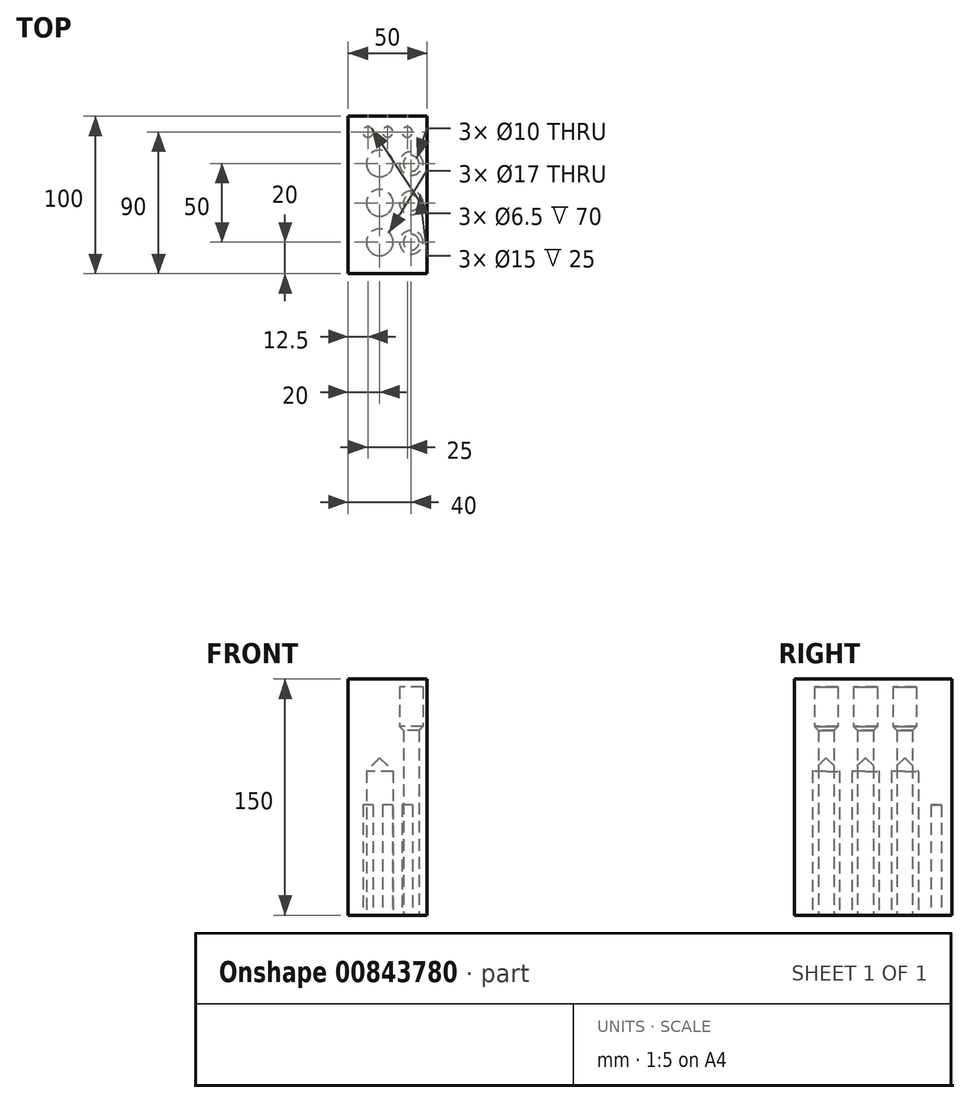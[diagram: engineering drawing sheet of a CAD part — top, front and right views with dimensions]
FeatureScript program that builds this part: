
annotation { "Feature Type Name" : "Feature", "Feature Type Description" : "" }
export const myFeature = defineFeature(function(context is Context, id is Id, definition is map)
    precondition{}
    {
        {
            var Q0;
            Q0=qCreatedBy(makeId("Top.planeOp"),FACE);
            var sketch = newSketch(context, id + "F0", { "sketchPlane" : qUnion([Q0])});
            skLineSegment(sketch, "E0.bottom", {"start": v(0, 100) * mm, "end": v(50, 100) * mm});
            skLineSegment(sketch, "E0.top", {"start": v(0, 0) * mm, "end": v(50, 0) * mm});
            skLineSegment(sketch, "E0.left", {"start": v(0, 100) * mm, "end": v(0, 0) * mm});
            skLineSegment(sketch, "E0.right", {"start": v(50, 100) * mm, "end": v(50, 0) * mm});
            skCircle(sketch, "E1", {"center": v(20, 45) * mm, "radius": 8.5 * mm});
            skCircle(sketch, "E2", {"center": v(20, 70) * mm, "radius": 8.5 * mm});
            skCircle(sketch, "E3", {"center": v(20, 20) * mm, "radius": 8.5 * mm});
            skCircle(sketch, "E4", {"center": v(40, 20) * mm, "radius": 5 * mm});
            skCircle(sketch, "E5", {"center": v(40, 45) * mm, "radius": 5 * mm});
            skCircle(sketch, "E6", {"center": v(40, 70) * mm, "radius": 5 * mm});
            skCircle(sketch, "E7", {"center": v(12.5, 90) * mm, "radius": 3.25 * mm});
            skCircle(sketch, "E8", {"center": v(37.5, 90) * mm, "radius": 3.25 * mm});
            skCircle(sketch, "E9", {"center": v(25, 90) * mm, "radius": 3.25 * mm});
            skSolve(sketch);
        }
        {
            var Q0;
            Q0=makeQuery(id+"F0.imprint","IMPRINT",FACE,{"disambiguationData":[TD([[makeQuery(id+"F0.imprint","IMPRINT",EDGE,{"derivedFrom":sQuery(id+"F0.wireOp",EDGE,"E0.bottom")}),-1.0]])]});
            var Q1;
            Q1=makeQuery(id+"F0.imprint","IMPRINT",FACE,{"disambiguationData":[TD([[makeQuery(id+"F0.imprint","IMPRINT",EDGE,{"derivedFrom":sQuery(id+"F0.wireOp",EDGE,"E7")}),1.0]])]});
            var Q2;
            Q2=makeQuery(id+"F0.imprint","IMPRINT",FACE,{"disambiguationData":[TD([[makeQuery(id+"F0.imprint","IMPRINT",EDGE,{"derivedFrom":sQuery(id+"F0.wireOp",EDGE,"E9")}),1.0]])]});
            var Q3;
            Q3=makeQuery(id+"F0.imprint","IMPRINT",FACE,{"disambiguationData":[TD([[makeQuery(id+"F0.imprint","IMPRINT",EDGE,{"derivedFrom":sQuery(id+"F0.wireOp",EDGE,"E8")}),1.0]])]});
            var Q4;
            Q4=makeQuery(id+"F0.imprint","IMPRINT",FACE,{"disambiguationData":[TD([[makeQuery(id+"F0.imprint","IMPRINT",EDGE,{"derivedFrom":sQuery(id+"F0.wireOp",EDGE,"E6")}),1.0]])]});
            var Q5;
            Q5=makeQuery(id+"F0.imprint","IMPRINT",FACE,{"disambiguationData":[TD([[makeQuery(id+"F0.imprint","IMPRINT",EDGE,{"derivedFrom":sQuery(id+"F0.wireOp",EDGE,"E2")}),1.0]])]});
            var Q6;
            Q6=makeQuery(id+"F0.imprint","IMPRINT",FACE,{"disambiguationData":[TD([[makeQuery(id+"F0.imprint","IMPRINT",EDGE,{"derivedFrom":sQuery(id+"F0.wireOp",EDGE,"E5")}),1.0]])]});
            var Q7;
            Q7=makeQuery(id+"F0.imprint","IMPRINT",FACE,{"disambiguationData":[TD([[makeQuery(id+"F0.imprint","IMPRINT",EDGE,{"derivedFrom":sQuery(id+"F0.wireOp",EDGE,"E4")}),1.0]])]});
            var Q8;
            Q8=makeQuery(id+"F0.imprint","IMPRINT",FACE,{"disambiguationData":[TD([[makeQuery(id+"F0.imprint","IMPRINT",EDGE,{"derivedFrom":sQuery(id+"F0.wireOp",EDGE,"E3")}),1.0]])]});
            var Q9;
            Q9=makeQuery(id+"F0.imprint","IMPRINT",FACE,{"disambiguationData":[TD([[makeQuery(id+"F0.imprint","IMPRINT",EDGE,{"derivedFrom":sQuery(id+"F0.wireOp",EDGE,"E1")}),1.0]])]});
            extrude(context, id + "F1", {"entities" : qUnion([Q0, Q1, Q2, Q3, Q4, Q5, Q6, Q7, Q8, Q9]), "depth" : 150 * mm, "offsetDistance" : 25 * mm});
        }
        {
            var Q0;
            Q0=makeQuery(id+"F0.imprint","IMPRINT",FACE,{"disambiguationData":[TD([[makeQuery(id+"F0.imprint","IMPRINT",EDGE,{"derivedFrom":sQuery(id+"F0.wireOp",EDGE,"E3")}),1.0]])]});
            var Q1;
            Q1=makeQuery(id+"F0.imprint","IMPRINT",FACE,{"disambiguationData":[TD([[makeQuery(id+"F0.imprint","IMPRINT",EDGE,{"derivedFrom":sQuery(id+"F0.wireOp",EDGE,"E1")}),1.0]])]});
            var Q2;
            Q2=makeQuery(id+"F0.imprint","IMPRINT",FACE,{"disambiguationData":[TD([[makeQuery(id+"F0.imprint","IMPRINT",EDGE,{"derivedFrom":sQuery(id+"F0.wireOp",EDGE,"E2")}),1.0]])]});
            extrude(context, id + "F2", {"entities" : qUnion([Q0, Q1, Q2]), "operationType" : NewBodyOperationType.REMOVE, "depth" : 100 * mm, "offsetDistance" : 25 * mm});
        }
        {
            var Q0;
            Q0=makeQuery(id+"F0.imprint","IMPRINT",FACE,{"disambiguationData":[TD([[makeQuery(id+"F0.imprint","IMPRINT",EDGE,{"derivedFrom":sQuery(id+"F0.wireOp",EDGE,"E8")}),1.0]])]});
            var Q1;
            Q1=makeQuery(id+"F0.imprint","IMPRINT",FACE,{"disambiguationData":[TD([[makeQuery(id+"F0.imprint","IMPRINT",EDGE,{"derivedFrom":sQuery(id+"F0.wireOp",EDGE,"E9")}),1.0]])]});
            var Q2;
            Q2=makeQuery(id+"F0.imprint","IMPRINT",FACE,{"disambiguationData":[TD([[makeQuery(id+"F0.imprint","IMPRINT",EDGE,{"derivedFrom":sQuery(id+"F0.wireOp",EDGE,"E7")}),1.0]])]});
            extrude(context, id + "F3", {"entities" : qUnion([Q0, Q1, Q2]), "operationType" : NewBodyOperationType.REMOVE, "depth" : 70 * mm, "offsetDistance" : 25 * mm});
        }
        {
            var Q0;
            Q0=makeQuery(id+"F0.imprint","IMPRINT",FACE,{"disambiguationData":[TD([[makeQuery(id+"F0.imprint","IMPRINT",EDGE,{"derivedFrom":sQuery(id+"F0.wireOp",EDGE,"E4")}),1.0]])]});
            var Q1;
            Q1=makeQuery(id+"F0.imprint","IMPRINT",FACE,{"disambiguationData":[TD([[makeQuery(id+"F0.imprint","IMPRINT",EDGE,{"derivedFrom":sQuery(id+"F0.wireOp",EDGE,"E5")}),1.0]])]});
            var Q2;
            Q2=makeQuery(id+"F0.imprint","IMPRINT",FACE,{"disambiguationData":[TD([[makeQuery(id+"F0.imprint","IMPRINT",EDGE,{"derivedFrom":sQuery(id+"F0.wireOp",EDGE,"E6")}),1.0]])]});
            extrude(context, id + "F4", {"entities" : qUnion([Q0, Q1, Q2]), "operationType" : NewBodyOperationType.REMOVE, "depth" : 130 * mm, "offsetDistance" : 25 * mm});
        }
        {
            var Q0;
            Q0=makeQuery(id+"F1.opExtrude","SWEPT_FACE",FACE,{"disambiguationData":[OSD([sQuery(id+"F0.wireOp",EDGE,"E0.left")])]});
            var sketch = newSketch(context, id + "F5", { "sketchPlane" : qUnion([Q0])});
            skLineSegment(sketch, "E10", {"start": v(0, 150) * mm, "end": v(0, 130) * mm});
            skLineSegment(sketch, "E11", {"start": v(-100, 150) * mm, "end": v(-100, 130) * mm});
            skSolve(sketch);
        }
        {
            var Q0;
            Q0=makeQuery(id+"F1.opExtrude","SWEPT_FACE",FACE,{"disambiguationData":[OSD([sQuery(id+"F0.wireOp",EDGE,"E0.right")])]});
            var sketch = newSketch(context, id + "F6", { "sketchPlane" : qUnion([Q0])});
            skLineSegment(sketch, "E12", {"start": v(100, 150) * mm, "end": v(100, 130) * mm});
            skSolve(sketch);
        }
        {
            var Q0;
            Q0=sQuery(id+"F5.wireOp",VERTEX,"E11.end");
            var Q1;
            Q1=sQuery(id+"F6.wireOp",VERTEX,"E12.end");
            var Q2;
            Q2=sQuery(id+"F5.wireOp",VERTEX,"E10.end");
            cPlane(context, id + "F7", {"entities" : qUnion([Q0, Q1, Q2]), "cplaneType" : CPlaneType.THREE_POINT, "offset" : 25 * mm, "width" : 150 * mm, "height" : 150 * mm});
        }
        {
            var Q0;
            Q0=qCreatedBy(id+"F7.planeOp",FACE);
            var sketch = newSketch(context, id + "F8", { "sketchPlane" : qUnion([Q0])});
            skCircle(sketch, "E13", {"center": v(40, 70) * mm, "radius": 7.5 * mm});
            skCircle(sketch, "E14", {"center": v(40, 45) * mm, "radius": 7.5 * mm});
            skCircle(sketch, "E15", {"center": v(40, 20) * mm, "radius": 7.5 * mm});
            skSolve(sketch);
        }
        {
            var Q0;
            Q0 = qSketchRegion(id + "F8", true);
            extrude(context, id + "F9", {"entities" : qUnion([Q0]), "operationType" : NewBodyOperationType.REMOVE, "depth" : 30 * mm, "offsetDistance" : 25 * mm, "symmetric" : true});
        }
        {
            var Q0;
            Q0=makeQuery(id+"F9.boolean.opBoolean","COPY",EDGE,{"derivedFrom":makeQuery(id+"F9.opExtrude","CAP_EDGE",EDGE,{"disambiguationData":[OSD([sQuery(id+"F8.wireOp",EDGE,"E13")])],"isStart":true})});
            var Q1;
            Q1=makeQuery(id+"F9.boolean.opBoolean","COPY",EDGE,{"derivedFrom":makeQuery(id+"F9.opExtrude","CAP_EDGE",EDGE,{"disambiguationData":[OSD([sQuery(id+"F8.wireOp",EDGE,"E14")])],"isStart":true})});
            var Q2;
            Q2=makeQuery(id+"F9.boolean.opBoolean","COPY",EDGE,{"derivedFrom":makeQuery(id+"F9.opExtrude","CAP_EDGE",EDGE,{"disambiguationData":[OSD([sQuery(id+"F8.wireOp",EDGE,"E15")])],"isStart":true})});
            chamfer(context, id + "F10", {"entities" : qUnion([Q0, Q1, Q2]), "width" : 5 * mm, "tangentPropagation" : true});
        }
        {
            var Q0;
            Q0=makeQuery(id+"F2.boolean.opBoolean","COPY",EDGE,{"derivedFrom":makeQuery(id+"F2.opExtrude","CAP_EDGE",EDGE,{"disambiguationData":[OSD([sQuery(id+"F0.wireOp",EDGE,"E2")])],"isStart":false})});
            var Q1;
            Q1=makeQuery(id+"F2.boolean.opBoolean","COPY",EDGE,{"derivedFrom":makeQuery(id+"F2.opExtrude","CAP_EDGE",EDGE,{"disambiguationData":[OSD([sQuery(id+"F0.wireOp",EDGE,"E1")])],"isStart":false})});
            var Q2;
            Q2=makeQuery(id+"F2.boolean.opBoolean","COPY",EDGE,{"derivedFrom":makeQuery(id+"F2.opExtrude","CAP_EDGE",EDGE,{"disambiguationData":[OSD([sQuery(id+"F0.wireOp",EDGE,"E3")])],"isStart":false})});
            chamfer(context, id + "F11", {"entities" : qUnion([Q0, Q1, Q2]), "width" : 8.5 * mm, "tangentPropagation" : true});
        }
    });
